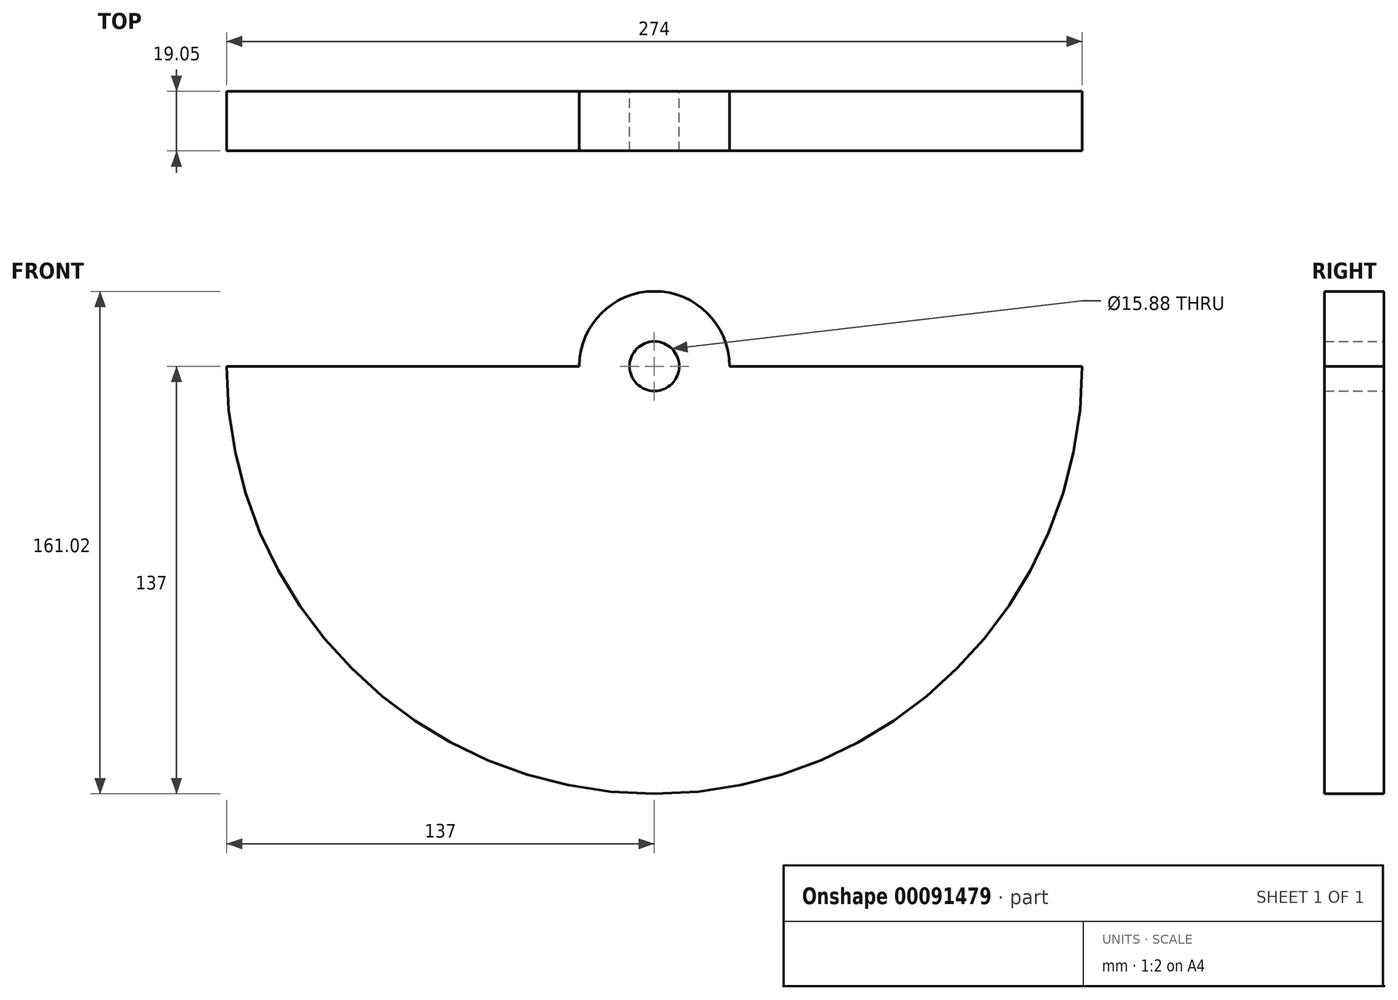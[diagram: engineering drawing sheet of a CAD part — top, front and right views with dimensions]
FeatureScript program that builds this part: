
annotation { "Feature Type Name" : "Feature", "Feature Type Description" : "" }
export const myFeature = defineFeature(function(context is Context, id is Id, definition is map)
    precondition{}
    {
        {
            var Q0;
            Q0=qCreatedBy(makeId("Front.planeOp"),FACE);
            var sketch = newSketch(context, id + "F0", { "sketchPlane" : qUnion([Q0])});
            skArc(sketch, "E0", {"start": v(-137, 0) * mm, "mid": v(0, -137) * mm, "end": v(137, 0) * mm});
            skLineSegment(sketch, "E1", {"start": v(0, 0) * mm, "end": v(24.02, 0) * mm});
            skLineSegment(sketch, "E2", {"start": v(0, 0) * mm, "end": v(-24.02, 0) * mm});
            skCircle(sketch, "E3", {"center": v(0, 0) * mm, "radius": 7.94 * mm});
            skArc(sketch, "E4", {"start": v(24.02, 0) * mm, "mid": v(0, 24.02) * mm, "end": v(-24.02, 0) * mm});
            skLineSegment(sketch, "E5", {"start": v(-24.02, 0) * mm, "end": v(-137, 0) * mm});
            skLineSegment(sketch, "E6", {"start": v(24.02, 0) * mm, "end": v(137, 0) * mm});
            skSolve(sketch);
        }
        {
            var Q0;
            Q0=makeQuery(id+"F0.imprint","IMPRINT",FACE,{"disambiguationData":[TD([[makeQuery(id+"F0.imprint","IMPRINT",EDGE,{"derivedFrom":sQuery(id+"F0.wireOp",EDGE,"E0")}),1.0]])]});
            var Q1;
            {var subQ0=sQuery(id+"F0.wireOp",EDGE,"E4");Q1=makeQuery(id+"F0.imprint","IMPRINT",FACE,{"disambiguationData":[TD([[makeQuery(id+"F0.imprint","IMPRINT",EDGE,{"derivedFrom":subQ0}),1.0]])]});}
            extrude(context, id + "F1", {"entities" : qUnion([Q0, Q1]), "depth" : 19.05 * mm});
        }
    });
